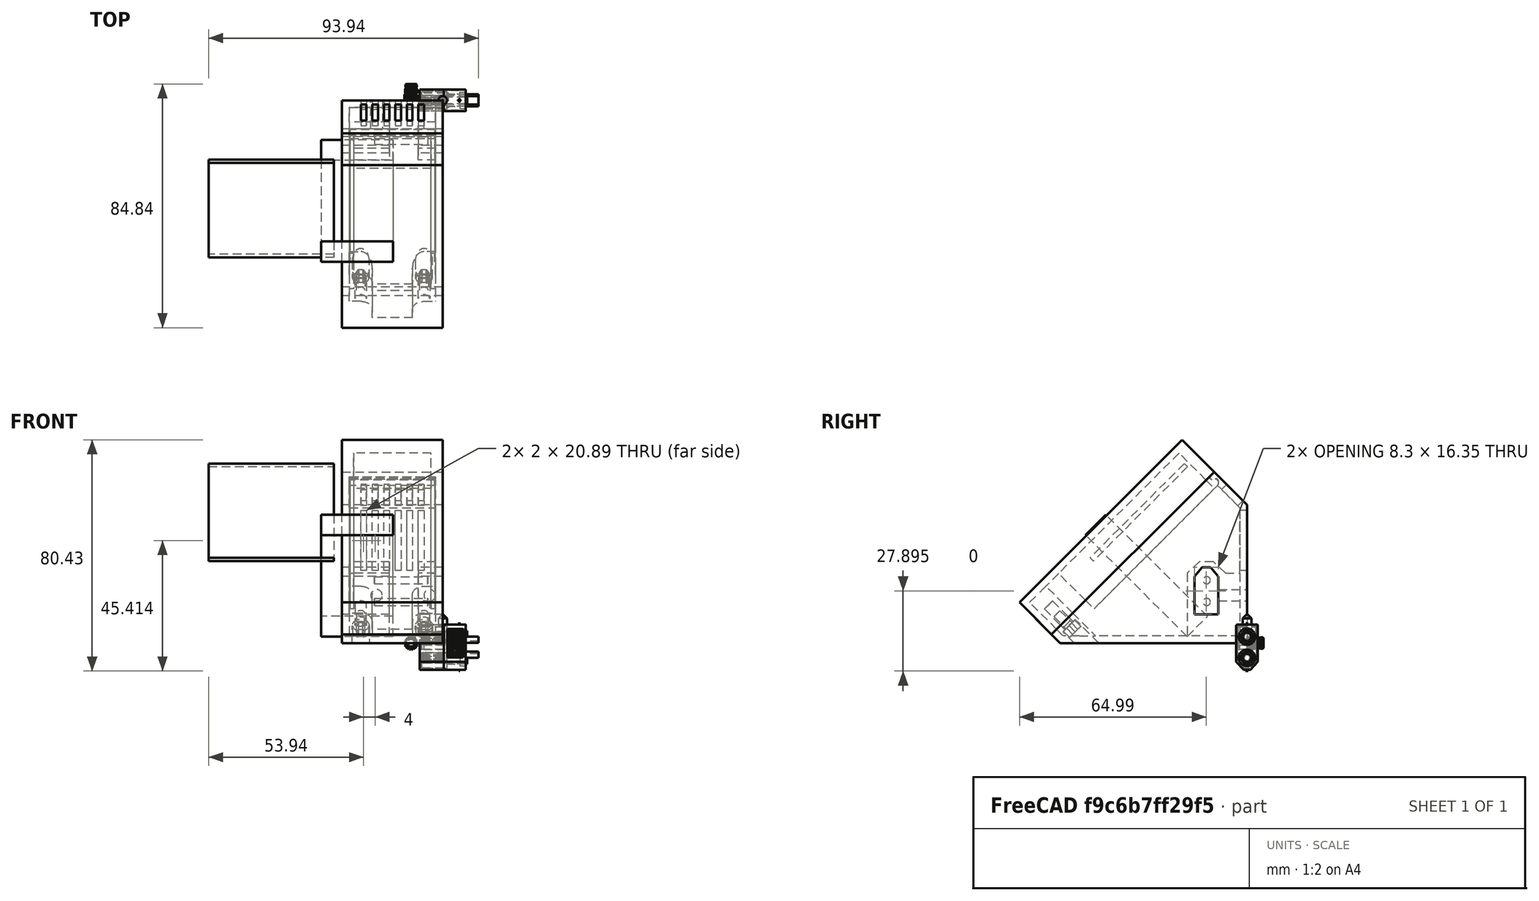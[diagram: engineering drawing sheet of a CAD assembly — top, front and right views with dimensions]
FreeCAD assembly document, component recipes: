
FREECAD ASSEMBLY — COMPONENT RECIPES ("moduleUSB_SimpleDual_00_SurBase35mm_012")

This assembly document has 13 components, labeled P0..P12 below (a component is one placed body or linked part). 6 of them carry a construction recipe — the FreeCAD feature program that regenerates the part from scratch, quoted from this document or its linked companion documents; the rest are supplied as boundary geometry only. No exploded tour is included for this assembly.
COMPONENT P0 — recipe-attached ("base", modeled in this document).
Construction recipe (the document's own serialized feature program — sketch geometry with constraints, then the solid features built on it; lengths are millimeters unless a unit is written):

FEATURE [PartDesign::FeatureBase] Clone
  BaseFeature = -> Slice_child0
FEATURE [PartDesign::Thickness] Thickness
  Base = -> Clone [Face7]
  BaseFeature = -> Clone
  Intersection = false
  Join = 0
  Mode = 0
  Reversed = true
  SupportTransform = false
  Value = 2.5
  expr: Value = <<sp>>.epaisseurParois
FEATURE [PartDesign::Plane] DatumPlane001  label="planXt"
  AttachmentOffset = pos=(0,0,-2.5) rot=(0,0,1;0rad)
  Length = 110.737
  MapMode = 5
  Placement = pos=(-2.5,6e-16,-6e-16) rot=(0.57735,0.57735,0.57735;2.0944rad)
  ResizeMode = 0
  Support = -> [YZ_Plane002]
  Width = 102.305
  expr: .AttachmentOffset.Base.z = -<<sp>>.epaisseurParois
FEATURE [Sketcher::SketchObject] Sketch002  label="sk_renfortXt"
  FullyConstrained = true
  MapMode = 5
  Placement = pos=(-2.5,6e-16,-6e-16) rot=(0.57735,0.57735,0.57735;2.0944rad)
  Support = -> [DatumPlane001]
  expr: .Constraints.dist = <<sp>>.xt60distanceAngleBord
  expr: .Constraints.epRf = <<sp>>.xt60epRenfort
  expr: Constraints[13] = <<sp>>.xt60largeurFetiere
  expr: Constraints[14] = <<sp>>.xt60hauteur
  expr: Constraints[15] = <<sp>>.xt60hauteurToit
  expr: Constraints[16] = <<sp>>.xt60base
  expr: Constraints[18] = .Constraints.dist
  expr: Constraints[31] = <<sp>>.epaisseurParois
  expr: Constraints[32] = .Constraints.epRf
  expr: Constraints[34] = .Constraints.epRf
  expr: Constraints[45] = <<sp>>.epaisseurParois
  sketch-geometry (17):
    g0: LineSegment StartX=-18.3 StartY=10 StartZ=0 EndX=-18.3 EndY=23.25 EndZ=0
    g1: LineSegment StartX=-18.3 StartY=23.25 StartZ=0 EndX=-15.65 EndY=25.75 EndZ=0
    g2: LineSegment StartX=-15.65 StartY=25.75 StartZ=0 EndX=-12.65 EndY=25.75 EndZ=0
    g3: LineSegment StartX=-12.65 StartY=25.75 StartZ=0 EndX=-10 EndY=23.25 EndZ=0
    g4: LineSegment StartX=-10 StartY=23.25 StartZ=0 EndX=-10 EndY=10 EndZ=0
    g5: LineSegment StartX=-10 StartY=10 StartZ=0 EndX=-18.3 EndY=10 EndZ=0
    g6: LineSegment StartX=-14.15 StartY=10 StartZ=0 EndX=-14.15 EndY=25.75 EndZ=0
    g7: LineSegment StartX=-16.6431 StartY=28.25 StartZ=0 EndX=-20.8 EndY=24.3284 EndZ=0
    g8: LineSegment StartX=-20.8 StartY=24.3284 StartZ=0 EndX=-20.8 EndY=2.5 EndZ=0
    g9: LineSegment StartX=-20.8 StartY=2.5 StartZ=0 EndX=-7.5 EndY=2.5 EndZ=0
    g10: LineSegment StartX=-7.5 StartY=2.5 StartZ=0 EndX=-7.5 EndY=24.3284 EndZ=0
    g11: LineSegment StartX=-7.5 StartY=24.3284 StartZ=0 EndX=-11.6569 EndY=28.25 EndZ=0
    g12: LineSegment StartX=-11.6569 StartY=28.25 StartZ=0 EndX=-16.6431 EndY=28.25 EndZ=0
    g13: LineSegment StartX=-7.5 StartY=24.3284 StartZ=0 EndX=-2.5 EndY=24.3284 EndZ=0
    g14: LineSegment StartX=-2.5 StartY=24.3284 StartZ=0 EndX=-2.5 EndY=2.5 EndZ=0
    g15: LineSegment StartX=-2.5 StartY=2.5 StartZ=0 EndX=-7.5 EndY=2.5 EndZ=0
    g16: LineSegment StartX=-7.5 StartY=2.5 StartZ=0 EndX=-7.5 EndY=24.3284 EndZ=0
  constraints (46):
    c: Vertical(g0)
    c: Coincident(g0,g1)
    c: Coincident(g1,g2)
    c: Horizontal(g2)
    c: Coincident(g2,g3)
    c: Coincident(g3,g4)
    c: Vertical(g4)
    c: Coincident(g4,g5)
    c: Coincident(g5,g0)
    c: Horizontal(g5)
    c: Symmetric(g1,g2,g6)
    c: Equal(g0,g4)
    c: Symmetric(g0,g4,g6)
    c: DistanceX(g2,g2) = 3
    c: DistanceY(g4,g4) = 13.25
    c: DistanceY(g3,g2) = 2.5
    c: DistanceX(g5,g5) = 8.3
    c: DistanceX(g4,g-1) = 10  'dist'
    c: DistanceY(g-1,g4) = 10
    c: Coincident(g7,g8)
    c: Vertical(g8)
    c: Coincident(g8,g9)
    c: Horizontal(g9)
    c: Coincident(g9,g10)
    c: Coincident(g10,g11)
    c: Coincident(g11,g12)
    c: Coincident(g12,g7)
    c: Symmetric(g7,g10,g6)
    c: Symmetric(g7,g11,g6)
    c: Symmetric(g8,g9,g6)
    c: DistanceX(g8,g0) = 2.5  'epRf'
    c: DistanceY(g-1,g9) = 2.5
    c: Distance(g7,g1) = 2.5
    c: Parallel(g1,g7)
    c: DistanceY(g2,g11) = 2.5
    c: Coincident(g13,g14)
    c: Coincident(g14,g15)
    c: Coincident(g15,g16)
    c: Coincident(g16,g13)
    c: Horizontal(g13)
    c: Horizontal(g15)
    c: Vertical(g14)
    c: Vertical(g16)
    c: Coincident(g13,g11)
    c: Horizontal(g14,g9)
    c: DistanceX(g14,g-1) = 2.5
FEATURE [PartDesign::Pad] Pad001  label="renfortXt"
  AllowMultiFace = false
  BaseFeature = -> Thickness
  Direction = (1,-1e-16,1e-16)
  Length = 30
  Length2 = 100
  Profile = -> Sketch002
  Reversed = true
  Type = 0
  expr: Length = <<sp>>.largeurModuleBase - 2 * <<sp>>.epaisseurParois
FEATURE [Sketcher::SketchObject] Sketch003  label="sk_trouXt"
  FullyConstrained = true
  MapMode = 5
  Placement = pos=(0,0,0) rot=(0.57735,0.57735,0.57735;2.0944rad)
  Support = -> [YZ_Plane002]
  expr: .Constraints.dist = <<sp>>.xt60distanceAngleBord
  expr: Constraints[13] = <<sp>>.xt60base
  expr: Constraints[14] = <<sp>>.xt60hauteur
  expr: Constraints[15] = <<sp>>.xt60hauteurToit + <<sp>>.xtJeu
  expr: Constraints[16] = <<sp>>.xt60largeurFetiere
  expr: Constraints[18] = .Constraints.dist
  sketch-geometry (7):
    g0: LineSegment StartX=-18.3 StartY=10 StartZ=0 EndX=-18.3 EndY=23.25 EndZ=0
    g1: LineSegment StartX=-18.3 StartY=23.25 StartZ=0 EndX=-15.65 EndY=26.35 EndZ=0
    g2: LineSegment StartX=-15.65 StartY=26.35 StartZ=0 EndX=-12.65 EndY=26.35 EndZ=0
    g3: LineSegment StartX=-12.65 StartY=26.35 StartZ=0 EndX=-10 EndY=23.25 EndZ=0
    g4: LineSegment StartX=-10 StartY=23.25 StartZ=0 EndX=-10 EndY=10 EndZ=0
    g5: LineSegment StartX=-10 StartY=10 StartZ=0 EndX=-18.3 EndY=10 EndZ=0
    g6: LineSegment StartX=-14.15 StartY=10 StartZ=0 EndX=-14.15 EndY=26.35 EndZ=0
  constraints (19):
    c: Vertical(g0)
    c: Coincident(g0,g1)
    c: Coincident(g1,g2)
    c: Horizontal(g2)
    c: Coincident(g2,g3)
    c: Coincident(g3,g4)
    c: Coincident(g4,g5)
    c: Coincident(g5,g0)
    c: Horizontal(g5)
    c: Symmetric(g1,g2,g6)
    c: Symmetric(g0,g3,g6)
    c: Vertical(g6)
    c: Symmetric(g0,g4,g6)
    c: DistanceX(g5,g5) = 8.3
    c: DistanceY(g4,g4) = 13.25
    c: DistanceY(g3,g2) = 3.1
    c: DistanceX(g2,g2) = 3
    c: DistanceX(g4,g-1) = 10  'dist'
    c: DistanceY(g-1,g4) = 10
FEATURE [PartDesign::Pocket] Pocket
  AllowMultiFace = false
  BaseFeature = -> Pad001
  Direction = (-1,2e-16,-3e-16)
  Length = 35
  Length2 = 100
  Profile = -> Sketch003
  Type = 0
  expr: Length = <<sp>>.largeurModuleBase
FEATURE [PartDesign::Plane] DatumPlane002  label="planDecoupeRenfortXt"
  AttachmentOffset = pos=(0,0,2.5) rot=(0,0,1;0rad)
  Length = 74.2466
  MapMode = 5
  Placement = pos=(0,-2.5,-6e-16) rot=(1,0,0;1.5708rad)
  ResizeMode = 0
  Support = -> [XZ_Plane002]
  Width = 98.8151
  expr: .AttachmentOffset.Base.z = <<sp>>.epaisseurParois
FEATURE [Sketcher::SketchObject] Sketch004  label="sk_decoupRenfXt"
  FullyConstrained = true
  MapMode = 5
  Placement = pos=(0,-2.5,-6e-16) rot=(1,0,0;1.5708rad)
  Support = -> [DatumPlane002]
  expr: Constraints[10] = <<sp>>.xt60LongueurRenfortPetit + <<sp>>.epaisseurParois
  expr: Constraints[11] = <<sp>>.largeurModuleBase - (<<sp>>.xt60longueurRenfortGrand + <<sp>>.epaisseurParois)
  expr: Constraints[8] = <<sp>>.epaisseurParois
  expr: Constraints[9] = <<sp>>.xt60distanceAngleBord + <<sp>>.xt60hauteur + <<sp>>.xt60hauteurToit + <<sp>>.xt60epRenfort
  sketch-geometry (4):
    g0: LineSegment StartX=-18.5 StartY=28.25 StartZ=0 EndX=-8.5 EndY=28.25 EndZ=0
    g1: LineSegment StartX=-8.5 StartY=28.25 StartZ=0 EndX=-8.5 EndY=2.5 EndZ=0
    g2: LineSegment StartX=-8.5 StartY=2.5 StartZ=0 EndX=-18.5 EndY=2.5 EndZ=0
    g3: LineSegment StartX=-18.5 StartY=2.5 StartZ=0 EndX=-18.5 EndY=28.25 EndZ=0
  constraints (12):
    c: Coincident(g0,g1)
    c: Coincident(g1,g2)
    c: Coincident(g2,g3)
    c: Coincident(g3,g0)
    c: Horizontal(g0)
    c: Horizontal(g2)
    c: Vertical(g1)
    c: Vertical(g3)
    c: DistanceY(g-1,g1) = 2.5
    c: DistanceY(g-1,g0) = 28.25
    c: DistanceX(g1,g-1) = 8.5
    c: DistanceX(g2,g-1) = 18.5
FEATURE [PartDesign::Pocket] Pocket001  label="decoupeRenfXt"
  AllowMultiFace = false
  BaseFeature = -> Pocket
  Direction = (0,1,2e-16)
  Length = 23.3
  Length2 = 100
  Profile = -> Sketch004
  Reversed = true
  Type = 0
  expr: Length = <<sp>>.xt60distanceAngleBord + <<sp>>.xt60base + 2 * <<sp>>.xt60epRenfort
FEATURE [Sketcher::SketchObject] Sketch005  label="xt60PercagePostMale"
  FullyConstrained = true
  MapMode = 5
  Placement = pos=(0,0,0) rot=(1,0,0;1.5708rad)
  Support = -> [XZ_Plane002]
  expr: Constraints[0] = <<sp>>.insertDiamPercage
  expr: Constraints[1] = <<sp>>.insertDistanceTrouBordMale
  expr: Constraints[2] = <<sp>>.insertHauteur
  sketch-geometry (1):
    g0: Circle CenterX=-4.5 CenterY=16.625 CenterZ=0 NormalX=0 NormalY=0 NormalZ=1 AngleXU=0 Radius=2
  constraints (3):
    c: Diameter(g0) = 4
    c: DistanceX(g0,g-1) = 4.5
    c: DistanceY(g-1,g0) = 16.625
FEATURE [PartDesign::Pocket] Pocket002  label="insertXtMale"
  AllowMultiFace = false
  BaseFeature = -> Pocket001
  Direction = (0,1,2e-16)
  Length = 10
  Length2 = 100
  Profile = -> Sketch005
  Reversed = true
  Type = 0
  expr: Length = <<sp>>.insertProfondeurPercage
FEATURE [Sketcher::SketchObject] Sketch006  label="xt60PercagePostFem"
  FullyConstrained = true
  MapMode = 5
  Placement = pos=(0,0,0) rot=(1,0,0;1.5708rad)
  Support = -> [XZ_Plane002]
  expr: Constraints[0] = <<sp>>.insertDiamPercage
  expr: Constraints[1] = <<sp>>.insertDistanceTrouBordFem
  expr: Constraints[2] = <<sp>>.insertHauteur
  sketch-geometry (1):
    g0: Circle CenterX=-23 CenterY=16.625 CenterZ=0 NormalX=0 NormalY=0 NormalZ=1 AngleXU=0 Radius=2
  constraints (3):
    c: Diameter(g0) = 4
    c: DistanceX(g0,g-1) = 23
    c: DistanceY(g-1,g0) = 16.625
FEATURE [PartDesign::Pocket] Pocket003  label="insertXt60Fem"
  AllowMultiFace = false
  BaseFeature = -> Pocket002
  Direction = (0,1,2e-16)
  Length = 10
  Length2 = 100
  Profile = -> Sketch006
  Reversed = true
  Type = 0
  expr: Length = <<sp>>.insertProfondeurPercage
FEATURE [PartDesign::Plane] DatumPlane003
  AttachmentOffset = pos=(0,0,2.5) rot=(0,0,1;0rad)
  Length = 74.9399
  MapMode = 2
  Placement = pos=(0,0,2.5) rot=(0,0,1;0rad)
  ResizeMode = 0
  Support = -> [XY_Plane002]
  Width = 107.94
  expr: .AttachmentOffset.Base.z = <<sp>>.epaisseurParois
FEATURE [PartDesign::Plane] DatumPlane004  label="planTrancheur"
  AttachmentOffset = pos=(0,0,71) rot=(-1,0,0;0.785398rad)
  Length = 77.3593
  MapMode = 5
  Placement = pos=(0,-71,-1.58e-14) rot=(1,0,0;0.785398rad)
  ResizeMode = 0
  Support = -> [XZ_Plane002]
  Width = 142.919
  expr: .AttachmentOffset.Base.z = <<sp>>.planTrancheur
FEATURE [Sketcher::SketchObject] Sketch008
  FullyConstrained = true
  MapMode = 5
  Placement = pos=(0,-71,-2.13e-14) rot=(1,0,0;0.785398rad)
  Support = -> [DatumPlane004]
  expr: .Constraints.dist = <<sp>>.epaisseurParois
  expr: Constraints[13] = <<sp>>.epaisseurParois
  expr: Constraints[16] = <<sp>>.insertDiamPercage / 2 + <<sp>>.insertFAVMargeDist
  expr: Constraints[1] = <<sp>>.insertFavDistAuZeroDuPLan
  expr: Constraints[21] = <<sp>>.insertFAVDistBord
  expr: Constraints[22] = <<sp>>.largeurModuleBase - <<sp>>.epaisseurParois
  sketch-geometry (7):
    g0: LineSegment StartX=-2.5 StartY=4.24264 StartZ=0 EndX=-32.5 EndY=4.24264 EndZ=0
    g1: LineSegment StartX=-6.5 StartY=14.7426 StartZ=0 EndX=-2.5 EndY=14.7426 EndZ=0
    g2: LineSegment StartX=-2.5 StartY=14.7426 StartZ=0 EndX=-2.5 EndY=6.74264 EndZ=0
    g3: LineSegment StartX=-2.5 StartY=6.74264 StartZ=0 EndX=-10.5 EndY=6.74264 EndZ=0
    g4: LineSegment StartX=-10.5 StartY=6.74264 StartZ=0 EndX=-10.5 EndY=10.7426 EndZ=0
    g5: ArcOfCircle CenterX=-6.5 CenterY=10.7426 CenterZ=0 NormalX=0 NormalY=0 NormalZ=1 AngleXU=0 Radius=4 StartAngle=1.5708 EndAngle=3.14159
    g6: LineSegment StartX=-6.5 StartY=10.7426 StartZ=0 EndX=-6.5 EndY=6.74264 EndZ=0
  constraints (23):
    c: Horizontal(g0)
    c: DistanceY(g-1,g0) = 4.24264
    c: DistanceX(g0,g-1) = 2.5  'dist'
    c: Horizontal(g1)
    c: Coincident(g1,g2)
    c: Vertical(g2)
    c: Coincident(g2,g3)
    c: Horizontal(g3)
    c: Coincident(g3,g4)
    c: Vertical(g4)
    c: Vertical(g2,g0)
    c: Equal(g3,g2)
    c: Equal(g4,g1)
    c: DistanceY(g0,g2) = 2.5
    c: Coincident(g5,g4)
    c: Coincident(g5,g1)
    c: DistanceX(g5,g2) = 4
    c: Coincident(g6,g5)
    c: PointOnObject(g6,g3)
    c: Vertical(g6)
    c: Vertical(g5,g1)
    c: DistanceX(g3,g3) = 8
    c: DistanceX(g0,g-1) = 32.5
FEATURE [PartDesign::Pad] Pad003  label="padTrouFAVDroite"
  AllowMultiFace = false
  BaseFeature = -> Pocket003
  Direction = (0,-0.707107,0.707107)
  Length = 10
  Length2 = 100
  Profile = -> Sketch008
  Reversed = true
  Type = 3
  UpToFace = -> DatumPlane003
FEATURE [Sketcher::SketchObject] Sketch009
  FullyConstrained = true
  MapMode = 5
  Placement = pos=(0,-71,-2.13e-14) rot=(1,0,0;0.785398rad)
  Support = -> [DatumPlane004]
  expr: .Constraints.larg = <<sp>>.insertFAVDistBord
  expr: Constraints[11] = .Constraints.larg / 2
  expr: Constraints[12] = <<sp>>.largeurModuleBase
  expr: Constraints[13] = <<sp>>.insertFavDistAuZeroDuPLan
  expr: Constraints[14] = <<sp>>.epaisseurParois
  expr: Constraints[15] = <<sp>>.epaisseurParois
  expr: Constraints[8] = .Constraints.larg
  sketch-geometry (6):
    g0: LineSegment StartX=-32.5 StartY=6.74264 StartZ=0 EndX=-24.5 EndY=6.74264 EndZ=0
    g1: LineSegment StartX=-24.5 StartY=6.74264 StartZ=0 EndX=-24.5 EndY=10.7426 EndZ=0
    g2: LineSegment StartX=-28.5 StartY=14.7426 StartZ=0 EndX=-32.5 EndY=14.7426 EndZ=0
    g3: LineSegment StartX=-32.5 StartY=14.7426 StartZ=0 EndX=-32.5 EndY=6.74264 EndZ=0
    g4: ArcOfCircle CenterX=-28.5 CenterY=10.7426 CenterZ=0 NormalX=0 NormalY=0 NormalZ=1 AngleXU=0 Radius=4 StartAngle=1e-16 EndAngle=1.5708
    g5: GeomPoint X=-35 Y=4.24264 Z=0
  constraints (16):
    c: Coincident(g0,g1)
    c: Coincident(g2,g3)
    c: Coincident(g3,g0)
    c: Horizontal(g0)
    c: Horizontal(g2)
    c: Vertical(g1)
    c: Vertical(g3)
    c: DistanceX(g0,g0) = 8  'larg'
    c: DistanceY(g3,g3) = 8
    c: Tangent(g2,g4) = -1.5708
    c: Tangent(g1,g4) = -1.5708
    c: DistanceX(g0,g4) = 4
    c: DistanceX(g5,g-1) = 35
    c: DistanceY(g-1,g5) = 4.24264
    c: DistanceX(g5,g0) = 2.5
    c: DistanceY(g5,g0) = 2.5
FEATURE [PartDesign::Pad] Pad004  label="padTrouFavGauche"
  AllowMultiFace = false
  BaseFeature = -> Pad003
  Direction = (0,-0.707107,0.707107)
  Length = 10
  Length2 = 100
  Profile = -> Sketch009
  Type = 3
  UpToFace = -> DatumPlane003 [Plane]
FEATURE [Sketcher::SketchObject] Sketch010
  FullyConstrained = true
  MapMode = 5
  Placement = pos=(0,-71,-2.13e-14) rot=(1,0,0;0.785398rad)
  Support = -> [DatumPlane004]
  expr: Constraints[0] = <<sp>>.insertFAVDistBord / 2 + <<sp>>.epaisseurParois
  expr: Constraints[1] = <<sp>>.insertFavDistAuZeroDuPLan + <<sp>>.epaisseurParois + <<sp>>.insertFAVDistBord / 2
  expr: Constraints[2] = <<sp>>.insertDiamPercage
  sketch-geometry (1):
    g0: Circle CenterX=-6.5 CenterY=10.7426 CenterZ=0 NormalX=0 NormalY=0 NormalZ=1 AngleXU=0 Radius=2
  constraints (3):
    c: DistanceX(g0,g-1) = 6.5
    c: DistanceY(g-1,g0) = 10.7426
    c: Diameter(g0) = 4
FEATURE [PartDesign::Pocket] Pocket004  label="trouDroit"
  AllowMultiFace = false
  BaseFeature = -> Pad004
  Direction = (0,0.707107,-0.707107)
  Length = 5
  Length2 = 100
  Profile = -> Sketch010
  Type = 1
FEATURE [Sketcher::SketchObject] Sketch011
  FullyConstrained = true
  MapMode = 5
  Placement = pos=(0,-71,-2.13e-14) rot=(1,0,0;0.785398rad)
  Support = -> [DatumPlane004]
  expr: Constraints[0] = <<sp>>.insertDiamPercage
  expr: Constraints[1] = <<sp>>.largeurModuleBase - <<sp>>.epaisseurParois - <<sp>>.insertFAVDistBord / 2
  expr: Constraints[2] = <<sp>>.insertFavDistAuZeroDuPLan + <<sp>>.epaisseurParois + <<sp>>.insertFAVDistBord / 2
  sketch-geometry (1):
    g0: Circle CenterX=-28.5 CenterY=10.7426 CenterZ=0 NormalX=0 NormalY=0 NormalZ=1 AngleXU=0 Radius=2
  constraints (3):
    c: Diameter(g0) = 4
    c: DistanceX(g0,g-1) = 28.5
    c: DistanceY(g-1,g0) = 10.7426
FEATURE [PartDesign::Pocket] Pocket005  label="trouGauche"
  AllowMultiFace = false
  BaseFeature = -> Pocket004
  Direction = (0,0.707107,-0.707107)
  Length = 5
  Length2 = 100
  Profile = -> Sketch011
  Type = 1
FEATURE [PartDesign::Plane] DatumPlane005  label="planTeteVisFav"
  AttachmentOffset = pos=(0,0,68) rot=(-1,0,0;0.785398rad)
  Length = 77.3593
  MapMode = 5
  Placement = pos=(0,-68,-1.51e-14) rot=(1,0,0;0.785398rad)
  ResizeMode = 0
  Support = -> [XZ_Plane002]
  Width = 142.919
  expr: .AttachmentOffset.Base.z = <<sp>>.planTrancheur - 3
FEATURE [Sketcher::SketchObject] Sketch012
  ExternalGeometry = -> [Pocket005]
  FullyConstrained = true
  MapMode = 5
  Placement = pos=(0,-68,-1.42e-14) rot=(1,0,0;0.785398rad)
  Support = -> [DatumPlane005]
  expr: Constraints[1] = <<sp>>.visM3DiamEncastrement
  sketch-geometry (2):
    g0: Circle CenterX=-6.5 CenterY=8.62132 CenterZ=0 NormalX=0 NormalY=0 NormalZ=1 AngleXU=0 Radius=3
    g1: Circle CenterX=-28.5 CenterY=8.62132 CenterZ=0 NormalX=0 NormalY=0 NormalZ=1 AngleXU=0 Radius=3
  constraints (4):
    c: Equal(g0,g1)
    c: Diameter(g1) = 6
    c: Coincident(g1,g-4)
    c: Coincident(g-3,g0)
FEATURE [PartDesign::Pocket] Pocket006  label="evidementTeteVisFav"
  AllowMultiFace = false
  BaseFeature = -> Pocket005
  Direction = (0,0.707107,-0.707107)
  Length = 20
  Length2 = 100
  Profile = -> Sketch012
  Type = 1
FEATURE [Sketcher::SketchObject] Sketch014
  FullyConstrained = true
  MapMode = 5
  Placement = pos=(0,0,0) rot=(1,0,0;1.5708rad)
  Support = -> [XZ_Plane002]
  expr: Constraints[12] = <<sp>>.xt60distanceAngleBord + <<sp>>.xt60hauteur + <<sp>>.ventilDistBordFente
  expr: Constraints[13] = <<sp>>.ventilLargeurFentes
  expr: Constraints[14] = <<sp>>.ventilEcartfente / 2
  expr: Constraints[15] = <<sp>>.hauteurDuDos - <<sp>>.ventilDistBordFente
  expr: Constraints[2] = <<sp>>.hauteurDuDos
  expr: Constraints[3] = <<sp>>.largeurModuleBase / 2
  sketch-geometry (5):
    g0: LineSegment StartX=-17.5 StartY=0 StartZ=0 EndX=-17.5 EndY=48.1371 EndZ=0
    g1: LineSegment StartX=-20.5 StartY=46.1371 StartZ=0 EndX=-18.5 EndY=46.1371 EndZ=0
    g2: LineSegment StartX=-18.5 StartY=46.1371 StartZ=0 EndX=-18.5 EndY=25.25 EndZ=0
    g3: LineSegment StartX=-18.5 StartY=25.25 StartZ=0 EndX=-20.5 EndY=25.25 EndZ=0
    g4: LineSegment StartX=-20.5 StartY=25.25 StartZ=0 EndX=-20.5 EndY=46.1371 EndZ=0
  constraints (16):
    c: PointOnObject(g0,g-1)
    c: Vertical(g0)
    c: DistanceY(g0,g0) = 48.1371
    c: DistanceX(g0,g-1) = 17.5
    c: Coincident(g1,g2)
    c: Coincident(g2,g3)
    c: Coincident(g3,g4)
    c: Coincident(g4,g1)
    c: Horizontal(g1)
    c: Horizontal(g3)
    c: Vertical(g2)
    c: Vertical(g4)
    c: DistanceY(g-1,g2) = 25.25
    c: DistanceX(g1,g1) = 2
    c: DistanceX(g2,g0) = 1
    c: DistanceY(g-1,g1) = 46.1371
FEATURE [PartDesign::Pocket] Pocket008  label="ventilFente1"
  AllowMultiFace = false
  BaseFeature = -> Pocket006
  Direction = (0,1,2e-16)
  Length = 2.5
  Length2 = 100
  Profile = -> Sketch014
  Reversed = true
  Type = 0
  expr: Length = <<sp>>.epaisseurParois
FEATURE [PartDesign::LinearPattern] LinearPattern  label="ventilDosRepeat1"
  BaseFeature = -> Pocket008
  Direction = -> Sketch014 [H_Axis]
  Length = 8
  Occurrences = 3
  Originals = -> [Pocket008]
  Reversed = true
  expr: Length = <<sp>>.ventilLargeurRepet
  expr: Occurrences = <<sp>>.ventilNbrFents
FEATURE [PartDesign::LinearPattern] LinearPattern001  label="ventilDosRepeat2"
  BaseFeature = -> LinearPattern
  Direction = -> Sketch014 [H_Axis]
  Length = 12
  Occurrences = 4
  Originals = -> [Pocket008]
  expr: Length = <<sp>>.ventilLargeurRepet + <<sp>>.ventilEcartfente + <<sp>>.ventilLargeurFentes
  expr: Occurrences = <<sp>>.ventilNbrFents + 1
FEATURE [PartDesign::Plane] DatumPlane006  label="planVentilSup"
  AttachmentOffset = pos=(0,0,-48.1371) rot=(1,0,0;0.785398rad)
  Length = 77.3593
  MapMode = 5
  Placement = pos=(0,48.1371,1.07e-14) rot=(1,0,0;2.35619rad)
  ResizeMode = 0
  Support = -> [XZ_Plane002]
  Width = 142.919
  expr: .AttachmentOffset.Base.z = -<<sp>>.hauteurDuDos
FEATURE [Sketcher::SketchObject] Sketch015
  FullyConstrained = true
  MapMode = 5
  Placement = pos=(0,48.1371,1.07e-14) rot=(1,0,0;2.35619rad)
  Support = -> [DatumPlane006]
  expr: Constraints[10] = <<sp>>.ventilLargeurFentes
  expr: Constraints[11] = (<<sp>>.largeurModuleBase + <<sp>>.ventilEcartfente) / 2
  expr: Constraints[8] = <<sp>>.distanceAuZeroPlanBorArriere + <<sp>>.ventilDistBordFente
  expr: Constraints[9] = <<sp>>.longPetitRetSupSansFav - 2 * <<sp>>.ventilDistBordFente - <<sp>>.favBordureProf
  sketch-geometry (4):
    g0: LineSegment StartX=-18.5 StartY=78.0926 StartZ=0 EndX=-20.5 EndY=78.0926 EndZ=0
    g1: LineSegment StartX=-20.5 StartY=78.0926 StartZ=0 EndX=-20.5 EndY=70.0761 EndZ=0
    g2: LineSegment StartX=-20.5 StartY=70.0761 StartZ=0 EndX=-18.5 EndY=70.0761 EndZ=0
    g3: LineSegment StartX=-18.5 StartY=70.0761 StartZ=0 EndX=-18.5 EndY=78.0926 EndZ=0
  constraints (12):
    c: Coincident(g0,g1)
    c: Coincident(g1,g2)
    c: Coincident(g2,g3)
    c: Coincident(g3,g0)
    c: Horizontal(g0)
    c: Horizontal(g2)
    c: Vertical(g1)
    c: Vertical(g3)
    c: DistanceY(g-1,g2) = 70.0761
    c: DistanceY(g2,g0) = 8.01652
    c: DistanceX(g0,g0) = 2
    c: DistanceX(g2,g-1) = 18.5
FEATURE [PartDesign::Pocket] Pocket009  label="ventilSupFente"
  AllowMultiFace = false
  BaseFeature = -> LinearPattern001
  Direction = (0,0.707107,0.707107)
  Length = 5
  Length2 = 100
  Profile = -> Sketch015
  Reversed = true
  Type = 0
FEATURE [PartDesign::LinearPattern] LinearPattern002  label="ventilSupRepeat1"
  BaseFeature = -> Pocket009
  Direction = -> Sketch015 [H_Axis]
  Length = 8
  Occurrences = 3
  Originals = -> [Pocket009]
  Reversed = true
  expr: Length = <<sp>>.ventilLargeurRepet
  expr: Occurrences = <<sp>>.ventilNbrFents
FEATURE [PartDesign::LinearPattern] LinearPattern003  label="ventilSupRepeat2"
  BaseFeature = -> LinearPattern002
  Direction = -> Sketch015 [H_Axis]
  Length = 12
  Occurrences = 4
  Originals = -> [Pocket009]
  expr: Length = <<sp>>.ventilLargeurRepet + <<sp>>.ventilEcartfente + <<sp>>.ventilLargeurFentes
  expr: Occurrences = <<sp>>.ventilNbrFents + 1
FEATURE [PartDesign::Body] Body001  label="base"
  BaseFeature = -> Slice_child0
  Group = -> [Clone,Thickness,DatumPlane001,Sketch002,Pad001,Sketch003,Pocket,DatumPlane002,Sketch004,Pocket001,Sketch005,Pocket002,Sketch006,Pocket003,DatumPlane003,DatumPlane004,Sketch008,Pad003,Sketch009,Pad004,Sketch010,Pocket004,Sketch011,Pocket005,DatumPlane005,Sketch012,Pocket006,Sketch014,Pocket008,LinearPattern,LinearPattern001,DatumPlane006,Sketch015,Pocket009,LinearPattern002,LinearPattern003,+3 more]
  Origin = -> Origin002
  Tip = -> Pocket015
COMPONENT P1 — recipe-attached ("faceAvant", modeled in this document).
Construction recipe (the document's own serialized feature program — sketch geometry with constraints, then the solid features built on it; lengths are millimeters unless a unit is written):

FEATURE [PartDesign::FeatureBase] Clone001
  BaseFeature = -> Slice_child1
FEATURE [PartDesign::Thickness] Thickness001
  Base = -> Clone001 [Face5]
  BaseFeature = -> Clone001
  Intersection = false
  Join = 0
  Mode = 0
  Reversed = true
  SupportTransform = false
  Value = 2.5
  expr: Value = <<sp>>.epaisseurParois
FEATURE [PartDesign::Plane] DatumPlane007  label="planTrancheurBis"
  AttachmentOffset = pos=(0,0,71) rot=(-1,0,0;0.785398rad)
  Length = 78.4163
  MapMode = 5
  Placement = pos=(0,-71,-1.58e-14) rot=(1,0,0;0.785398rad)
  ResizeMode = 0
  Support = -> [XZ_Plane003]
  Width = 159.734
  expr: .AttachmentOffset.Base.z = <<sp>>.planTrancheur
FEATURE [Sketcher::SketchObject] Sketch016  label="sk_insertFavDroit"
  FullyConstrained = true
  MapMode = 5
  Placement = pos=(0,-71,-2.13e-14) rot=(1,0,0;0.785398rad)
  Support = -> [DatumPlane007]
  expr: Constraints[11] = <<sp>>.insertFAVDistBord
  expr: Constraints[14] = <<sp>>.insertFAVDistBord / 2
  expr: Constraints[7] = <<sp>>.epaisseurParois
  expr: Constraints[8] = <<sp>>.insertFavDistAuZeroDuPLan + <<sp>>.epaisseurParois
  expr: Constraints[9] = <<sp>>.insertFAVDistBord
  sketch-geometry (5):
    g0: LineSegment StartX=-6.5 StartY=14.7426 StartZ=0 EndX=-2.5 EndY=14.7426 EndZ=0
    g1: LineSegment StartX=-2.5 StartY=14.7426 StartZ=0 EndX=-2.5 EndY=6.74264 EndZ=0
    g2: LineSegment StartX=-2.5 StartY=6.74264 StartZ=0 EndX=-10.5 EndY=6.74264 EndZ=0
    g3: LineSegment StartX=-10.5 StartY=6.74264 StartZ=0 EndX=-10.5 EndY=10.7426 EndZ=0
    g4: ArcOfCircle CenterX=-6.5 CenterY=10.7426 CenterZ=0 NormalX=0 NormalY=0 NormalZ=1 AngleXU=0 Radius=4 StartAngle=1.5708 EndAngle=3.14159
  constraints (15):
    c: Horizontal(g0)
    c: Coincident(g0,g1)
    c: Vertical(g1)
    c: Coincident(g1,g2)
    c: Horizontal(g2)
    c: Coincident(g2,g3)
    c: Vertical(g3)
    c: DistanceX(g1,g-1) = 2.5
    c: DistanceY(g-1,g1) = 6.74264
    c: DistanceY(g1,g1) = 8
    c: Equal(g3,g0)
    c: DistanceX(g2,g2) = 8
    c: Coincident(g4,g0)
    c: Tangent(g4,g3) = 1.5708
    c: DistanceX(g4,g1) = 4
FEATURE [PartDesign::Pad] Pad005  label="padInsertFavDroit"
  AllowMultiFace = false
  BaseFeature = -> Thickness001
  Direction = (0,-0.707107,0.707107)
  Length = 10
  Length2 = 100
  Profile = -> Sketch016
  Type = 2
FEATURE [Sketcher::SketchObject] Sketch017  label="sp_padInserFavGauch"
  FullyConstrained = true
  MapMode = 5
  Placement = pos=(0,-71,-2.13e-14) rot=(1,0,0;0.785398rad)
  Support = -> [DatumPlane007]
  expr: Constraints[10] = <<sp>>.insertFAVDistBord
  expr: Constraints[12] = <<sp>>.insertFAVDistBord / 2
  expr: Constraints[13] = <<sp>>.largeurModuleBase
  expr: Constraints[14] = <<sp>>.insertFavDistAuZeroDuPLan
  expr: Constraints[15] = <<sp>>.epaisseurParois
  expr: Constraints[16] = <<sp>>.epaisseurParois
  sketch-geometry (6):
    g0: LineSegment StartX=-28.5 StartY=14.7426 StartZ=0 EndX=-32.5 EndY=14.7426 EndZ=0
    g1: LineSegment StartX=-32.5 StartY=14.7426 StartZ=0 EndX=-32.5 EndY=6.74264 EndZ=0
    g2: LineSegment StartX=-32.5 StartY=6.74264 StartZ=0 EndX=-24.5 EndY=6.74264 EndZ=0
    g3: LineSegment StartX=-24.5 StartY=6.74264 StartZ=0 EndX=-24.5 EndY=10.7426 EndZ=0
    g4: ArcOfCircle CenterX=-28.5 CenterY=10.7426 CenterZ=0 NormalX=0 NormalY=0 NormalZ=1 AngleXU=0 Radius=4 StartAngle=0 EndAngle=1.5708
    g5: GeomPoint X=-35 Y=4.24264 Z=0
  constraints (17):
    c: Horizontal(g0)
    c: Coincident(g0,g1)
    c: Vertical(g1)
    c: Coincident(g1,g2)
    c: Horizontal(g2)
    c: Coincident(g2,g3)
    c: Vertical(g3)
    c: Equal(g3,g0)
    c: Equal(g2,g1)
    c: Coincident(g0,g4)
    c: DistanceX(g2,g2) = 8
    c: Tangent(g4,g3) = -1.5708
    c: DistanceX(g0,g0) = 4
    c: DistanceX(g5,g-1) = 35
    c: DistanceY(g-1,g5) = 4.24264
    c: DistanceY(g5,g1) = 2.5
    c: DistanceX(g5,g1) = 2.5
FEATURE [PartDesign::Pad] Pad006  label="padInsertFavGauch"
  AllowMultiFace = false
  BaseFeature = -> Pad005
  Direction = (0,-0.707107,0.707107)
  Length = 10
  Length2 = 100
  Profile = -> Sketch017
  Type = 2
FEATURE [Sketcher::SketchObject] Sketch018  label="skPercageInsertFavDroit"
  FullyConstrained = true
  MapMode = 5
  Placement = pos=(0,-71,-2.13e-14) rot=(1,0,0;0.785398rad)
  Support = -> [DatumPlane007]
  expr: Constraints[0] = <<sp>>.insertDiamPercage
  expr: Constraints[1] = <<sp>>.insertFavDistAuZeroDuPLan + <<sp>>.epaisseurParois + <<sp>>.insertFAVDistBord / 2
  expr: Constraints[2] = <<sp>>.epaisseurParois + <<sp>>.insertFAVDistBord / 2
  expr: Constraints[7] = <<sp>>.largeurModuleBase - 2 * <<sp>>.epaisseurParois - <<sp>>.insertFAVDistBord
  sketch-geometry (3):
    g0: Circle CenterX=-6.5 CenterY=10.7426 CenterZ=0 NormalX=0 NormalY=0 NormalZ=1 AngleXU=0 Radius=2
    g1: Circle CenterX=-28.5 CenterY=10.7426 CenterZ=0 NormalX=0 NormalY=0 NormalZ=1 AngleXU=0 Radius=2
    g2: LineSegment StartX=-28.5 StartY=10.7426 StartZ=0 EndX=-6.5 EndY=10.7426 EndZ=0
  constraints (8):
    c: Diameter(g0) = 4
    c: DistanceY(g-1,g0) = 10.7426
    c: DistanceX(g0,g-1) = 6.5
    c: Equal(g0,g1)
    c: Coincident(g2,g1)
    c: Coincident(g2,g0)
    c: Horizontal(g2)
    c: DistanceX(g2,g2) = 22
FEATURE [PartDesign::Pocket] Pocket010  label="trouInsertFavDroit"
  AllowMultiFace = false
  BaseFeature = -> Pad006
  Direction = (0,0.707107,-0.707107)
  Length = 8
  Length2 = 100
  Profile = -> Sketch018
  Reversed = true
  Type = 0
  expr: Length = <<sp>>.insertFavProfondeur
FEATURE [PartDesign::Plane] DatumPlane011  label="planFaceAvant"
  AttachmentOffset = pos=(0,0,93.2843) rot=(-1,0,0;0.785398rad)
  Length = 78.4163
  MapMode = 5
  Placement = pos=(0,-93.2843,-2.07e-14) rot=(1,0,0;0.785398rad)
  ResizeMode = 0
  Support = -> [XZ_Plane003]
  Width = 159.734
  expr: .AttachmentOffset.Base.z = <<sp>>.planFaceAvant
FEATURE [Sketcher::SketchObject] Sketch030  label="sk_rebordFav"
  FullyConstrained = true
  MapMode = 5
  Placement = pos=(0,-71,-2.13e-14) rot=(1,0,0;0.785398rad)
  Support = -> [DatumPlane007]
  expr: Constraints[0] = <<sp>>.insertFavDistAuZeroDuPLan
  expr: Constraints[19] = <<sp>>.epaisseurParois
  expr: Constraints[20] = <<sp>>.favEpBordure
  expr: Constraints[21] = <<sp>>.favDistBordPlan
  expr: Constraints[22] = <<sp>>.largeurModuleBase - 2 * <<sp>>.epaisseurParois
  expr: Constraints[23] = <<sp>>.favEpBordure
  expr: Constraints[24] = <<sp>>.Face - <<sp>>.epaisseurParois
  expr: Constraints[25] = <<sp>>.favEpBordure
  sketch-geometry (9):
    g0: GeomPoint X=2e-16 Y=4.24264 Z=0
    g1: LineSegment StartX=-32.5 StartY=20.9853 StartZ=0 EndX=-32.5 EndY=81.7426 EndZ=0
    g2: LineSegment StartX=-32.5 StartY=81.7426 StartZ=0 EndX=-2.5 EndY=81.7426 EndZ=0
    g3: LineSegment StartX=-2.5 StartY=81.7426 StartZ=0 EndX=-2.5 EndY=20.9853 EndZ=0
    g4: LineSegment StartX=-2.5 StartY=20.9853 StartZ=0 EndX=-4 EndY=20.9853 EndZ=0
    g5: LineSegment StartX=-4 StartY=20.9853 StartZ=0 EndX=-4 EndY=80.2426 EndZ=0
    g6: LineSegment StartX=-4 StartY=80.2426 StartZ=0 EndX=-31 EndY=80.2426 EndZ=0
    g7: LineSegment StartX=-31 StartY=80.2426 StartZ=0 EndX=-31 EndY=20.9853 EndZ=0
    g8: LineSegment StartX=-31 StartY=20.9853 StartZ=0 EndX=-32.5 EndY=20.9853 EndZ=0
  constraints (26):
    c: DistanceY(g-1,g0) = 4.24264
    c: Vertical(g0,g-1)
    c: Vertical(g1)
    c: Coincident(g1,g2)
    c: Horizontal(g2)
    c: Coincident(g2,g3)
    c: Vertical(g3)
    c: Coincident(g3,g4)
    c: Horizontal(g4)
    c: Coincident(g4,g5)
    c: Vertical(g5)
    c: Coincident(g5,g6)
    c: Horizontal(g6)
    c: Coincident(g6,g7)
    c: Vertical(g7)
    c: Coincident(g7,g8)
    c: Coincident(g8,g1)
    c: Horizontal(g8)
    c: Horizontal(g7,g4)
    c: DistanceX(g3,g0) = 2.5
    c: DistanceX(g4,g4) = 1.5
    c: DistanceY(g0,g3) = 16.7426
    c: DistanceX(g1,g3) = 30
    c: DistanceY(g5,g2) = 1.5
    c: DistanceY(g0,g2) = 77.5
    c: DistanceX(g1,g7) = 1.5
FEATURE [PartDesign::Pad] Pad014  label="favRebordSupport"
  AllowMultiFace = false
  BaseFeature = -> Pocket010
  Direction = (0,-0.707107,0.707107)
  Length = 10
  Length2 = 100
  Profile = -> Sketch030
  Type = 3
  UpToFace = -> Pocket010 [Face13]
FEATURE [PartDesign::Pad] Pad015  label="favRebord"
  AllowMultiFace = false
  BaseFeature = -> Pad014
  Direction = (0,-0.707107,0.707107)
  Length = 4.15
  Length2 = 100
  Profile = -> Sketch030
  Reversed = true
  Type = 0
  expr: Length = <<sp>>.favBordureProf
FEATURE [Sketcher::SketchObject] Sketch031  label="sk_bourlet"
  ExternalGeometry = -> [Pad015]
  FullyConstrained = true
  MapMode = 5
  Placement = pos=(-2.5,0,0) rot=(0.57735,0.57735,0.57735;2.0944rad)
  Support = -> [Pad015]
  expr: Constraints[3] = <<sp>>.bourletMaintientRayon - <<sp>>.bourletRayonJeu
  sketch-geometry (2):
    g0: ArcOfCircle CenterX=-11.184 CenterY=55.7855 CenterZ=0 NormalX=0 NormalY=0 NormalZ=1 AngleXU=0 Radius=1.3 StartAngle=5.49779 EndAngle=8.63938
    g1: LineSegment StartX=-12.1032 StartY=56.7048 StartZ=0 EndX=-10.2647 EndY=54.8663 EndZ=0
  constraints (6):
    c: Coincident(g0,g-3)
    c: PointOnObject(g0,g-3)
    c: PointOnObject(g0,g-3)
    c: Radius(g0) = 1.3
    c: Coincident(g1,g0)
    c: Coincident(g1,g0)
FEATURE [PartDesign::Pad] Pad016  label="bourlet"
  AllowMultiFace = false
  BaseFeature = -> Pad015
  Direction = (1,0,0)
  Length = 10
  Length2 = 100
  Profile = -> Sketch031
  Reversed = true
  Type = 3
  UpToFace = -> Pad015 [Face11]
FEATURE [Sketcher::SketchObject] Sketch039
  FullyConstrained = true
  MapMode = 5
  Placement = pos=(0,-71,-2.13e-14) rot=(1,0,0;0.785398rad)
  Support = -> [DatumPlane007]
  expr: Constraints[20] = <<sp>>.favBordureJeu / 2
  expr: Constraints[21] = <<sp>>.epaisseurParois
  expr: Constraints[22] = <<sp>>.largeurModuleBase - 2 * <<sp>>.epaisseurParois
  expr: Constraints[23] = <<sp>>.insertFavDistAuZeroDuPLan + <<sp>>.favDistBordPlan
  expr: Constraints[27] = <<sp>>.insertFavDistAuZeroDuPLan + <<sp>>.Face - <<sp>>.epaisseurParois + <<sp>>.bourletMaintientRayon
  sketch-geometry (10):
    g0: LineSegment StartX=-32.5 StartY=83.2426 StartZ=0 EndX=-32.25 EndY=83.2426 EndZ=0
    g1: LineSegment StartX=-32.25 StartY=83.2426 StartZ=0 EndX=-32.25 EndY=20.9853 EndZ=0
    g2: LineSegment StartX=-32.25 StartY=20.9853 StartZ=0 EndX=-32.5 EndY=20.9853 EndZ=0
    g3: LineSegment StartX=-32.5 StartY=20.9853 StartZ=0 EndX=-32.5 EndY=83.2426 EndZ=0
    g4: LineSegment StartX=-2.5 StartY=83.2426 StartZ=0 EndX=-2.75 EndY=83.2426 EndZ=0
    g5: LineSegment StartX=-2.75 StartY=83.2426 StartZ=0 EndX=-2.75 EndY=20.9853 EndZ=0
    g6: LineSegment StartX=-2.75 StartY=20.9853 StartZ=0 EndX=-2.5 EndY=20.9853 EndZ=0
    g7: LineSegment StartX=-2.5 StartY=20.9853 StartZ=0 EndX=-2.5 EndY=83.2426 EndZ=0
    g8: LineSegment StartX=-32.25 StartY=20.9853 StartZ=0 EndX=-2.5 EndY=20.9853 EndZ=0
    g9: LineSegment StartX=-2.75 StartY=83.2426 StartZ=0 EndX=-32.25 EndY=83.2426 EndZ=0
  constraints (28):
    c: Coincident(g0,g1)
    c: Coincident(g1,g2)
    c: Coincident(g2,g3)
    c: Coincident(g3,g0)
    c: Horizontal(g0)
    c: Horizontal(g2)
    c: Vertical(g1)
    c: Vertical(g3)
    c: Coincident(g4,g5)
    c: Coincident(g5,g6)
    c: Coincident(g6,g7)
    c: Coincident(g7,g4)
    c: Horizontal(g4)
    c: Horizontal(g6)
    c: Vertical(g5)
    c: Vertical(g7)
    c: Coincident(g8,g1)
    c: Coincident(g8,g6)
    c: Horizontal(g8)
    c: Equal(g2,g6)
    c: DistanceX(g2,g2) = 0.25
    c: DistanceX(g6,g-1) = 2.5
    c: DistanceX(g2,g6) = 30
    c: DistanceY(g-1,g6) = 20.9853
    c: Coincident(g9,g4)
    c: Coincident(g9,g0)
    c: Horizontal(g9)
    c: DistanceY(g-1,g4) = 83.2426
FEATURE [PartDesign::Pocket] Pocket018  label="ajoutJeuLevreFav"
  BaseFeature = -> Pad016
  Direction = (0,0.707107,-0.707107)
  Length = 4.15
  Length2 = 5
  Profile = -> Sketch039
  ReferenceAxis = -> Sketch039 [N_Axis]
  Type = 0
  expr: Length = <<sp>>.favBordureProf
FEATURE [PartDesign::Plane] DatumPlane016  label="planFaceAvantPCB"
  AttachmentOffset = pos=(0,0,84.28) rot=(-1,0,0;0.785398rad)
  Length = 78.4163
  MapMode = 5
  Placement = pos=(0,-84.28,-1.87e-14) rot=(1,0,0;0.785398rad)
  ResizeMode = 0
  Support = -> [XZ_Plane003]
  Width = 159.734
FEATURE [Sketcher::SketchObject] Sketch044  label="pcbFavSk"
  FullyConstrained = false
  MapMode = 5
  Placement = pos=(0,-84.28,-1.42e-14) rot=(1,0,0;0.785398rad)
  Support = -> [DatumPlane016]
  sketch-geometry (4):
    g0: LineSegment StartX=-80.4521 StartY=87.0314 StartZ=0 EndX=-37.8912 EndY=87.0314 EndZ=0
    g1: LineSegment StartX=-37.8912 StartY=87.0314 StartZ=0 EndX=-37.8912 EndY=42.7351 EndZ=0
    g2: LineSegment StartX=-37.8912 StartY=42.7351 StartZ=0 EndX=-80.4521 EndY=42.7351 EndZ=0
    g3: LineSegment StartX=-80.4521 StartY=42.7351 StartZ=0 EndX=-80.4521 EndY=87.0314 EndZ=0
  constraints (8):
    c: Coincident(g0,g1)
    c: Coincident(g1,g2)
    c: Coincident(g2,g3)
    c: Coincident(g3,g0)
    c: Horizontal(g0)
    c: Horizontal(g2)
    c: Vertical(g1)
    c: Vertical(g3)
FEATURE [PartDesign::Body] Body002  label="faceAvant"
  BaseFeature = -> Slice_child1
  Group = -> [Clone001,Thickness001,DatumPlane007,Sketch016,Pad005,Sketch017,Pad006,Sketch018,Pocket010,DatumPlane011,Sketch030,Pad014,Pad015,Sketch031,Pad016,Sketch039,Pocket018,DatumPlane016,Sketch044]
  Origin = -> Origin003
  Tip = -> Pocket018
COMPONENT P2 — geometry summary ("theBoard"; no construction recipe available for this part):
  bounding box: 59.2 x 55.2 x 51.3 mm
  tessellated surface: 96,346 triangles
  volume: 9777 mm^3 (6% of its bounding box)
COMPONENT P3 — geometry summary ("dcdc_002"; no construction recipe available for this part):
  bounding box: 54.0 x 24.0 x 14.8 mm
  tessellated surface: 266,733 triangles
  volume: 4112 mm^3 (21% of its bounding box)
COMPONENT P4 — geometry summary ("usbFem001"; no construction recipe available for this part):
  bounding box: 22.8 x 17.0 x 15.8 mm
  tessellated surface: 90,788 triangles
  volume: 995 mm^3 (16% of its bounding box)
  symmetry: mirror-symmetric across its x mid-plane
COMPONENT P5 — geometry summary ("switch_002"; no construction recipe available for this part):
  bounding box: 19.2 x 16.9 x 10.5 mm
  tessellated surface: 316 triangles
  volume: 1179 mm^3 (35% of its bounding box)
  symmetry: mirror-symmetric across its x mid-plane
COMPONENT P6 — recipe-attached ("tigeLaiton001", modeled in this document).
Construction recipe (the document's own serialized feature program — sketch geometry with constraints, then the solid features built on it; lengths are millimeters unless a unit is written):

FEATURE [PartDesign::Plane] DatumPlane012  label="planBaseTige"
  AttachmentOffset = pos=(0,0,-5.18) rot=(0,0,1;0rad)
  Length = 60
  MapMode = 5
  Placement = pos=(-5.18,1.2e-15,-1.2e-15) rot=(0.57735,0.57735,0.57735;2.0944rad)
  ResizeMode = 0
  Support = -> [YZ_Plane012]
  Width = 60
  expr: .AttachmentOffset.Base.z = -<<tige>>.planBaseTigeposX
FEATURE [Sketcher::SketchObject] Sketch032  label="sk_tiges"
  FullyConstrained = true
  MapMode = 5
  Placement = pos=(-5.18,1.2e-15,-1.2e-15) rot=(0.57735,0.57735,0.57735;2.0944rad)
  Support = -> [DatumPlane012]
  expr: Constraints[0] = <<tige>>.tigeDiam
  expr: Constraints[1] = <<tige>>.tigePosY
  expr: Constraints[2] = <<tige>>.tigePosX
  sketch-geometry (1):
    g0: Circle CenterX=-14 CenterY=14.3 CenterZ=0 NormalX=0 NormalY=0 NormalZ=1 AngleXU=0 Radius=1.25
  constraints (3):
    c: Diameter(g0) = 2.5
    c: DistanceY(g-1,g0) = 14.3
    c: DistanceX(g0,g-1) = 14
FEATURE [PartDesign::Pad] Pad017  label="tigeBasse"
  AllowMultiFace = false
  Direction = (1,-1e-16,1e-16)
  Length = 18.62
  Length2 = 100
  Placement = pos=(-5.18,1.2e-15,-1.2e-15) rot=(0.57735,0.57735,0.57735;2.0944rad)
  Profile = -> Sketch032
  Reversed = true
  Type = 0
  expr: Length = <<tige>>.tigeLong
FEATURE [PartDesign::Body] Body007  label="tigeLaiton"
  Group = -> [DatumPlane012,Sketch032,Pad017]
  Origin = -> Origin016
  Tip = -> Pad017
FEATURE [PartDesign::Plane] DatumPlane013  label="planTige2"
  AttachmentOffset = pos=(0,0,-5.18) rot=(0,0,1;0rad)
  Length = 60
  MapMode = 5
  Placement = pos=(-5.18,1.2e-15,-1.2e-15) rot=(0.57735,0.57735,0.57735;2.0944rad)
  ResizeMode = 0
  Support = -> [YZ_Plane014]
  Width = 60
  expr: .AttachmentOffset.Base.z = -<<tige>>.planBaseTigeposX
FEATURE [Sketcher::SketchObject] Sketch033  label="sk_tige2"
  FullyConstrained = true
  MapMode = 5
  Placement = pos=(-5.18,1.2e-15,-1.2e-15) rot=(0.57735,0.57735,0.57735;2.0944rad)
  Support = -> [DatumPlane013]
  expr: Constraints[0] = <<tige>>.tigeDiam
  expr: Constraints[1] = <<tige>>.tigePosX
  expr: Constraints[2] = <<tige>>.tigePosY + <<tige>>.xtEcartBroches
  sketch-geometry (1):
    g0: Circle CenterX=-14 CenterY=21.86 CenterZ=0 NormalX=0 NormalY=0 NormalZ=1 AngleXU=0 Radius=1.25
  constraints (3):
    c: Diameter(g0) = 2.5
    c: DistanceX(g0,g-1) = 14
    c: DistanceY(g-1,g0) = 21.86
FEATURE [PartDesign::Pad] Pad018
  AllowMultiFace = false
  Direction = (1,-1e-16,1e-16)
  Length = 18.62
  Length2 = 100
  Placement = pos=(-5.18,1.2e-15,-1.2e-15) rot=(0.57735,0.57735,0.57735;2.0944rad)
  Profile = -> Sketch033
  Reversed = true
  Type = 0
  expr: Length = <<tige>>.tigeLong
FEATURE [PartDesign::Body] Body008  label="tige2"
  Group = -> [DatumPlane013,Sketch033,Pad018]
  Origin = -> Origin018
  Tip = -> Pad018
COMPONENT P7 — geometry summary ("xtVisInsertFix"; no construction recipe available for this part):
  bounding box: 20.2 x 17.7 x 16.6 mm
  tessellated surface: 21,960 triangles
  volume: 1306 mm^3 (22% of its bounding box)
COMPONENT P8 — geometry summary ("xtVisInertMob"; no construction recipe available for this part):
  bounding box: 20.5 x 17.8 x 16.5 mm
  tessellated surface: 31,880 triangles
  volume: 1060 mm^3 (18% of its bounding box)
COMPONENT P9 — recipe-attached ("visInsertFavFix", modeled in this document).
Construction recipe (the document's own serialized feature program — sketch geometry with constraints, then the solid features built on it; lengths are millimeters unless a unit is written):

FEATURE [Sketcher::SketchObject] Sketch034  label="Sketch"
  FullyConstrained = false
  MapMode = 5
  Support = -> [XY_Plane015]
  sketch-geometry (1):
    g0: Circle CenterX=0 CenterY=0 CenterZ=0 NormalX=0 NormalY=0 NormalZ=1 AngleXU=0 Radius=2.75
  constraints (2):
    c: Coincident(g0,g-1)
    c: Diameter(g0) = 5.5
FEATURE [PartDesign::Pad] Pad019  label="tete"
  AllowMultiFace = false
  Direction = (1,1,1)
  Length = 3
  Length2 = 100
  Profile = -> Sketch034
  Type = 0
FEATURE [Sketcher::SketchObject] Sketch001
  FullyConstrained = false
  MapMode = 5
  Placement = pos=(0,0,0) rot=(1,0,0;3.14159rad)
  Support = -> [Pad019]
  sketch-geometry (1):
    g0: Circle CenterX=0 CenterY=0 CenterZ=0 NormalX=0 NormalY=0 NormalZ=1 AngleXU=0 Radius=1.5
  constraints (2):
    c: Coincident(g0,g-1)
    c: Diameter(g0) = 3
FEATURE [PartDesign::Pad] Pad020  label="corps"
  AllowMultiFace = false
  BaseFeature = -> Pad019
  Direction = (1,1,1)
  Length = 6
  Length2 = 100
  Profile = -> Sketch001
  Type = 0
FEATURE [PartDesign::Plane] DatumPlane014
  AttachmentOffset = pos=(0,0,3) rot=(0,0,1;0rad)
  Length = 60
  MapMode = 5
  Placement = pos=(0,0,3) rot=(0,0,1;0rad)
  ResizeMode = 0
  Support = -> [XY_Plane015]
  Width = 60
FEATURE [Sketcher::SketchObject] Sketch035  label="Sketch002"
  FullyConstrained = false
  MapMode = 5
  Placement = pos=(0,0,3) rot=(0,0,1;0rad)
  Support = -> [DatumPlane014]
  sketch-geometry (7):
    g0: LineSegment StartX=0.721688 StartY=-1.25 StartZ=0 EndX=1.44338 EndY=1.0119e-12 EndZ=0
    g1: LineSegment StartX=1.44338 StartY=1.0119e-12 StartZ=0 EndX=0.721688 EndY=1.25 EndZ=0
    g2: LineSegment StartX=0.721688 StartY=1.25 StartZ=0 EndX=-0.721688 EndY=1.25 EndZ=0
    g3: LineSegment StartX=-0.721688 StartY=1.25 StartZ=0 EndX=-1.44338 EndY=8.689e-13 EndZ=0
    g4: LineSegment StartX=-1.44338 StartY=8.689e-13 StartZ=0 EndX=-0.721688 EndY=-1.25 EndZ=0
    g5: LineSegment StartX=-0.721688 StartY=-1.25 StartZ=0 EndX=0.721688 EndY=-1.25 EndZ=0
    g6: Circle CenterX=0 CenterY=0 CenterZ=0 NormalX=0 NormalY=0 NormalZ=1 AngleXU=0 Radius=1.44338
  constraints (16):
    c: Coincident(g0,g1)
    c: Coincident(g1,g2)
    c: Coincident(g2,g3)
    c: Coincident(g3,g4)
    c: Coincident(g4,g5)
    c: Coincident(g5,g0)
    c: Equal(g0, g1-g5) x5
    c: PointOnObject(g0,g6)
    c: PointOnObject(g1,g6)
    c: PointOnObject(g2,g6)
    c: PointOnObject(g3,g6)
    c: PointOnObject(g4,g6)
    c: PointOnObject(g5,g6)
    c: Coincident(g6,g-1)
    c: Horizontal(g2)
    c: DistanceY(g0,g1) = 2.5
FEATURE [PartDesign::Pocket] Pocket016  label="emprunte"
  AllowMultiFace = false
  BaseFeature = -> Pad020
  Direction = (1,1,1)
  Length = 4
  Length2 = 100
  Profile = -> Sketch035
  Type = 0
FEATURE [PartDesign::Body] Body009  label="visTHCM3x6_FAV001"
  Group = -> [Sketch034,Pad019,Sketch001,Pad020,DatumPlane014,Sketch035,Pocket016]
  Origin = -> Origin019
  Placement = pos=(-6.5,-61.8718,6.01041) rot=(1,0,0;3.92699rad)
  Tip = -> Pocket016
COMPONENT P10 — recipe-attached ("visInserFavMob", modeled in this document).
Construction recipe (the document's own serialized feature program — sketch geometry with constraints, then the solid features built on it; lengths are millimeters unless a unit is written):

FEATURE [Sketcher::SketchObject] Sketch036
  FullyConstrained = false
  MapMode = 5
  Support = -> [XY_Plane016]
  sketch-geometry (1):
    g0: Circle CenterX=0 CenterY=0 CenterZ=0 NormalX=0 NormalY=0 NormalZ=1 AngleXU=0 Radius=2.75
  constraints (2):
    c: Coincident(g0,g-1)
    c: Diameter(g0) = 5.5
FEATURE [PartDesign::Pad] Pad021  label="tete001"
  AllowMultiFace = false
  Direction = (1,1,1)
  Length = 3
  Length2 = 100
  Profile = -> Sketch036
  Type = 0
FEATURE [Sketcher::SketchObject] Sketch037
  FullyConstrained = false
  MapMode = 5
  Placement = pos=(0,0,0) rot=(1,0,0;3.14159rad)
  Support = -> [Pad021]
  sketch-geometry (1):
    g0: Circle CenterX=0 CenterY=0 CenterZ=0 NormalX=0 NormalY=0 NormalZ=1 AngleXU=0 Radius=1.5
  constraints (2):
    c: Coincident(g0,g-1)
    c: Diameter(g0) = 3
FEATURE [PartDesign::Pad] Pad022  label="corps001"
  AllowMultiFace = false
  BaseFeature = -> Pad021
  Direction = (1,1,1)
  Length = 6
  Length2 = 100
  Profile = -> Sketch037
  Type = 0
FEATURE [PartDesign::Plane] DatumPlane015
  AttachmentOffset = pos=(0,0,3) rot=(0,0,1;0rad)
  Length = 60
  MapMode = 5
  Placement = pos=(0,0,3) rot=(0,0,1;0rad)
  ResizeMode = 0
  Support = -> [XY_Plane016]
  Width = 60
FEATURE [Sketcher::SketchObject] Sketch038
  FullyConstrained = false
  MapMode = 5
  Placement = pos=(0,0,3) rot=(0,0,1;0rad)
  Support = -> [DatumPlane015]
  sketch-geometry (7):
    g0: LineSegment StartX=0.721688 StartY=-1.25 StartZ=0 EndX=1.44338 EndY=1.0119e-12 EndZ=0
    g1: LineSegment StartX=1.44338 StartY=1.0119e-12 StartZ=0 EndX=0.721688 EndY=1.25 EndZ=0
    g2: LineSegment StartX=0.721688 StartY=1.25 StartZ=0 EndX=-0.721688 EndY=1.25 EndZ=0
    g3: LineSegment StartX=-0.721688 StartY=1.25 StartZ=0 EndX=-1.44338 EndY=8.689e-13 EndZ=0
    g4: LineSegment StartX=-1.44338 StartY=8.689e-13 StartZ=0 EndX=-0.721688 EndY=-1.25 EndZ=0
    g5: LineSegment StartX=-0.721688 StartY=-1.25 StartZ=0 EndX=0.721688 EndY=-1.25 EndZ=0
    g6: Circle CenterX=0 CenterY=0 CenterZ=0 NormalX=0 NormalY=0 NormalZ=1 AngleXU=0 Radius=1.44338
  constraints (16):
    c: Coincident(g0,g1)
    c: Coincident(g1,g2)
    c: Coincident(g2,g3)
    c: Coincident(g3,g4)
    c: Coincident(g4,g5)
    c: Coincident(g5,g0)
    c: Equal(g0, g1-g5) x5
    c: PointOnObject(g0,g6)
    c: PointOnObject(g1,g6)
    c: PointOnObject(g2,g6)
    c: PointOnObject(g3,g6)
    c: PointOnObject(g4,g6)
    c: PointOnObject(g5,g6)
    c: Coincident(g6,g-1)
    c: Horizontal(g2)
    c: DistanceY(g0,g1) = 2.5
FEATURE [PartDesign::Pocket] Pocket017  label="emprunte001"
  AllowMultiFace = false
  BaseFeature = -> Pad022
  Direction = (1,1,1)
  Length = 4
  Length2 = 100
  Profile = -> Sketch038
  Type = 0
FEATURE [PartDesign::Body] Body010  label="visTHCM3x6_FAV002"
  Group = -> [Sketch036,Pad021,Sketch037,Pad022,DatumPlane015,Sketch038,Pocket017]
  Origin = -> Origin020
  Placement = pos=(-28.5,-61.8718,6.01041) rot=(1,0,0;3.92699rad)
  Tip = -> Pocket017
  expr: .Placement.Base.x = -(<<sp>>.largeurModuleBase - 6.5)
COMPONENT P11 — geometry summary ("poubelle"; no construction recipe available for this part):
  bounding box: 43.6 x 34.0 x 34.0 mm
  tessellated surface: 3,984 triangles
  volume: 4442 mm^3 (9% of its bounding box)
COMPONENT P12 — recipe-attached ("etudeLM2596HV", modeled in this document).
Construction recipe (the document's own serialized feature program — sketch geometry with constraints, then the solid features built on it; lengths are millimeters unless a unit is written):

FEATURE [PartDesign::Body] Body012
  Origin = -> Origin030
PROVENANCE & LICENSES
A FreeCAD (.FCStd) document from a public repository crawl; recipes are the document's own serialized feature recipes (and, for linked parts, companion documents' recipes).
License: as declared in the source repository (recorded in the dataset sidecar).
